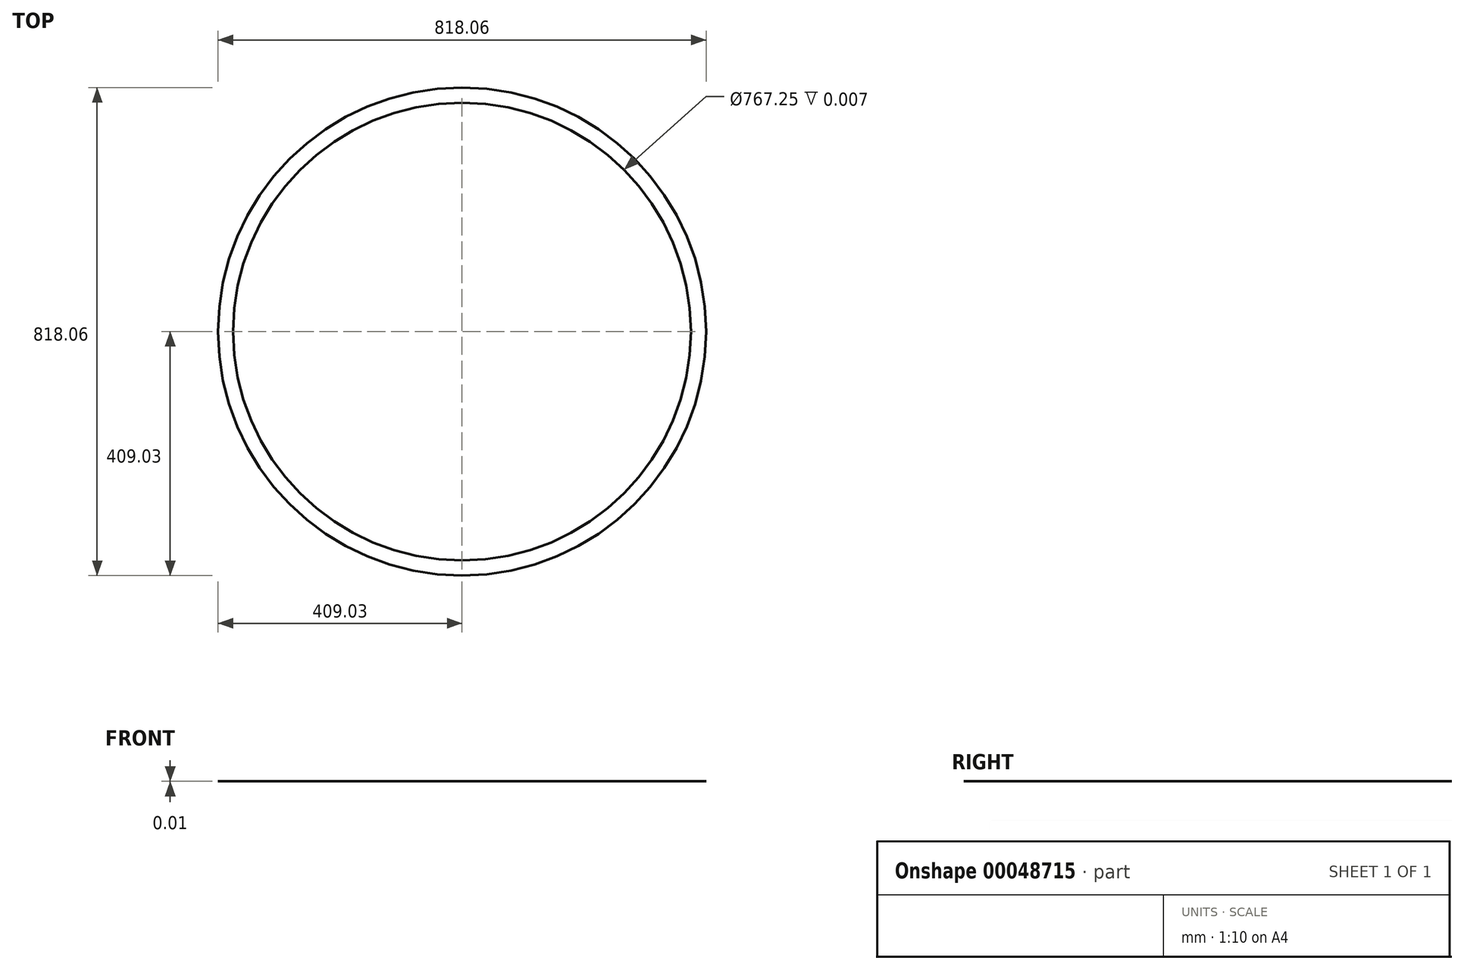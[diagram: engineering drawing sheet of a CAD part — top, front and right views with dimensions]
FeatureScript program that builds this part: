
annotation { "Feature Type Name" : "Feature", "Feature Type Description" : "" }
export const myFeature = defineFeature(function(context is Context, id is Id, definition is map)
    precondition{}
    {
        {
            var Q0;
            Q0=qCreatedBy(makeId("Top.planeOp"),FACE);
            var sketch = newSketch(context, id + "F0", { "sketchPlane" : qUnion([Q0])});
            skCircle(sketch, "E0", {"center": v(0, 0) * mm, "radius": 409.03 * mm});
            skCircle(sketch, "E1", {"center": v(0, 0) * mm, "radius": 383.63 * mm});
            skSolve(sketch);
        }
        {
            var Q0;
            Q0=makeQuery(id+"F0.imprint","IMPRINT",FACE,{"disambiguationData":[TD([[makeQuery(id+"F0.imprint","IMPRINT",EDGE,{"derivedFrom":sQuery(id+"F0.wireOp",EDGE,"E0")}),1.0]])]});
            extrude(context, id + "F1", {"entities" : qUnion([Q0]), "depth" : 3 / 406.4 * mm});
        }
    });
